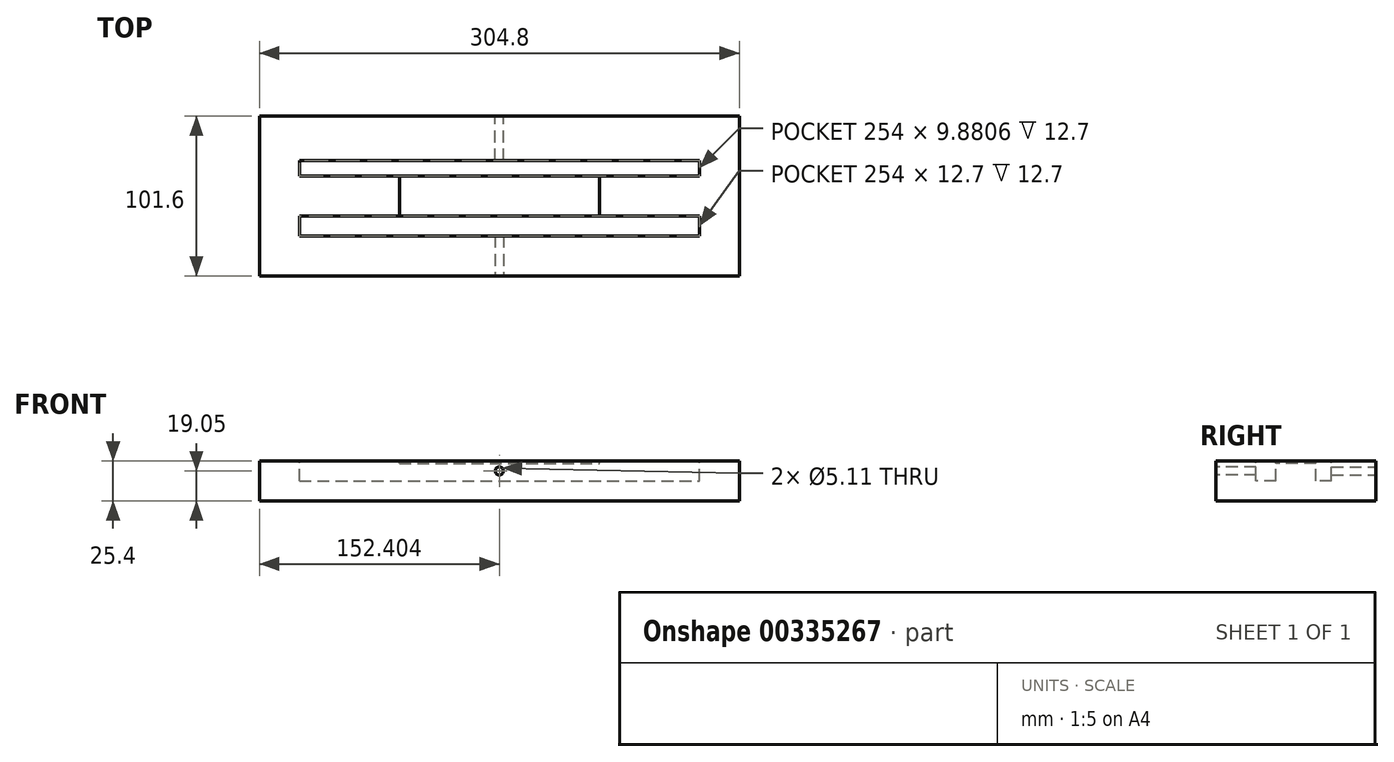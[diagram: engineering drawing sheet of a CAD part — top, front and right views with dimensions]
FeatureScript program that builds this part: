
annotation { "Feature Type Name" : "Feature", "Feature Type Description" : "" }
export const myFeature = defineFeature(function(context is Context, id is Id, definition is map)
    precondition{}
    {
        {
            var Q0;
            Q0=qCreatedBy(makeId("Top.planeOp"),FACE);
            var sketch = newSketch(context, id + "F0", { "sketchPlane" : qUnion([Q0])});
            skLineSegment(sketch, "E0.bottom", {"start": v(-47.49, 78.54) * mm, "end": v(257.31, 78.54) * mm});
            skLineSegment(sketch, "E0.top", {"start": v(-47.49, -23.06) * mm, "end": v(257.31, -23.06) * mm});
            skLineSegment(sketch, "E0.left", {"start": v(-47.49, 78.54) * mm, "end": v(-47.49, -23.06) * mm});
            skLineSegment(sketch, "E0.right", {"start": v(257.31, 78.54) * mm, "end": v(257.31, -23.06) * mm});
            skSolve(sketch);
        }
        {
            var Q0;
            Q0=makeQuery(id+"F0.imprint","IMPRINT",FACE,{"disambiguationData":[TD([[makeQuery(id+"F0.imprint","IMPRINT",EDGE,{"derivedFrom":sQuery(id+"F0.wireOp",EDGE,"E0.bottom")}),-1.0]])]});
            extrude(context, id + "F1", {"entities" : qUnion([Q0]), "depth" : 25.4 * mm});
        }
        {
            var Q0;
            Q0=makeQuery(id+"F1.opExtrude","CAP_FACE",FACE,{"disambiguationData":[OSD([sQuery(id+"F0.wireOp",EDGE,"E0.bottom"),sQuery(id+"F0.wireOp",EDGE,"E0.top"),sQuery(id+"F0.wireOp",EDGE,"E0.left"),sQuery(id+"F0.wireOp",EDGE,"E0.right")])],"isStart":false});
            var sketch = newSketch(context, id + "F2", { "sketchPlane" : qUnion([Q0])});
            skLineSegment(sketch, "E1.bottom", {"start": v(41.41, 40.44) * mm, "end": v(168.41, 40.44) * mm});
            skLineSegment(sketch, "E1.top", {"start": v(41.41, 15.04) * mm, "end": v(168.41, 15.04) * mm});
            skLineSegment(sketch, "E1.left", {"start": v(41.41, 40.44) * mm, "end": v(41.41, 15.04) * mm});
            skLineSegment(sketch, "E1.right", {"start": v(168.41, 40.44) * mm, "end": v(168.41, 15.04) * mm});
            skSolve(sketch);
        }
        {
            var Q0;
            Q0 = qSketchRegion(id + "F2", true);
            extrude(context, id + "F3", {"entities" : qUnion([Q0]), "operationType" : NewBodyOperationType.REMOVE, "oppositeDirection" : true, "depth" : 1.52 * mm});
        }
        {
            var Q0;
            Q0=makeQuery(id+"F1.opExtrude","CAP_FACE",FACE,{"disambiguationData":[OSD([sQuery(id+"F0.wireOp",EDGE,"E0.bottom"),sQuery(id+"F0.wireOp",EDGE,"E0.top"),sQuery(id+"F0.wireOp",EDGE,"E0.left"),sQuery(id+"F0.wireOp",EDGE,"E0.right")])],"isStart":false});
            var sketch = newSketch(context, id + "F4", { "sketchPlane" : qUnion([Q0])});
            skLineSegment(sketch, "E2.bottom", {"start": v(-22.09, 50.32) * mm, "end": v(231.91, 50.32) * mm});
            skLineSegment(sketch, "E2.top", {"start": v(-22.09, 40.44) * mm, "end": v(231.91, 40.44) * mm});
            skLineSegment(sketch, "E2.left", {"start": v(-22.09, 50.32) * mm, "end": v(-22.09, 40.44) * mm});
            skLineSegment(sketch, "E2.right", {"start": v(231.91, 50.32) * mm, "end": v(231.91, 40.44) * mm});
            skSolve(sketch);
        }
        {
            var Q0;
            Q0 = qSketchRegion(id + "F4", true);
            extrude(context, id + "F5", {"entities" : qUnion([Q0]), "operationType" : NewBodyOperationType.REMOVE, "oppositeDirection" : true, "depth" : 12.7 * mm});
        }
        {
            var Q0;
            Q0=makeQuery(id+"F1.opExtrude","CAP_FACE",FACE,{"disambiguationData":[OSD([sQuery(id+"F0.wireOp",EDGE,"E0.bottom"),sQuery(id+"F0.wireOp",EDGE,"E0.top"),sQuery(id+"F0.wireOp",EDGE,"E0.left"),sQuery(id+"F0.wireOp",EDGE,"E0.right")])],"isStart":false});
            var sketch = newSketch(context, id + "F6", { "sketchPlane" : qUnion([Q0])});
            skLineSegment(sketch, "E3.bottom", {"start": v(-22.09, 15.04) * mm, "end": v(231.91, 15.04) * mm});
            skLineSegment(sketch, "E3.top", {"start": v(-22.09, 2.34) * mm, "end": v(231.91, 2.34) * mm});
            skLineSegment(sketch, "E3.left", {"start": v(-22.09, 15.04) * mm, "end": v(-22.09, 2.34) * mm});
            skLineSegment(sketch, "E3.right", {"start": v(231.91, 15.04) * mm, "end": v(231.91, 2.34) * mm});
            skSolve(sketch);
        }
        {
            var Q0;
            Q0=makeQuery(id+"F6.imprint","IMPRINT",FACE,{"disambiguationData":[TD([[makeQuery(id+"F6.imprint","IMPRINT",EDGE,{"derivedFrom":sQuery(id+"F6.wireOp",EDGE,"E3.top")}),1.0]])]});
            extrude(context, id + "F7", {"entities" : qUnion([Q0]), "operationType" : NewBodyOperationType.REMOVE, "oppositeDirection" : true, "depth" : 12.7 * mm});
        }
        {
            var Q0;
            Q0=makeQuery(id+"F1.opExtrude","SWEPT_FACE",FACE,{"disambiguationData":[OSD([sQuery(id+"F0.wireOp",EDGE,"E0.top")])]});
            var sketch = newSketch(context, id + "F8", { "sketchPlane" : qUnion([Q0])});
            skPoint(sketch, "E4", {"position": v(104.91, 19.05) * mm});
            skPoint(sketch, "E4.positionSnap0", {"position": v(104.91, 25.4) * mm});
            skSolve(sketch);
        }
        {
            var Q0;
            Q0=sQuery(id+"F8.wireOp",VERTEX,"E4");
            var Q1;
            Q1=makeQuery(id+"F1.opExtrude","SWEPT_BODY",BODY,{"disambiguationData":[OSD([sQuery(id+"F0.wireOp",EDGE,"E0.bottom"),sQuery(id+"F0.wireOp",EDGE,"E0.top"),sQuery(id+"F0.wireOp",EDGE,"E0.left"),sQuery(id+"F0.wireOp",EDGE,"E0.right")])]});
            hole(context, id + "F9", {"style" : HoleStyle.SIMPLE, "endStyle" : HoleEndStyle.BLIND, "standardTappedOrClearance" : lookupTablePath({ "standard" : "ANSI", "engagement" : "75%", "pitch" : "20 tpi", "size" : "1/4", "type" : "Tapped" }), "standardBlindInLast" : lookupTablePath({ "standard" : "ANSI", "engagement" : "75%", "pitch" : "20 tpi", "size" : "1/4", "type" : "Tapped" }), "holeDiameter" : 5.1 * mm, "showTappedDepth" : true, "holeDepth" : 25.4 * mm, "tappedDepth" : 21.59 * mm, "tapClearance" : 3, "locations" : qUnion([Q0]), "scope" : qUnion([Q1]), "majorDiameter" : 6.35 * mm});
        }
        {
            var Q0;
            Q0=makeQuery(id+"F1.opExtrude","SWEPT_FACE",FACE,{"disambiguationData":[OSD([sQuery(id+"F0.wireOp",EDGE,"E0.bottom")])]});
            var sketch = newSketch(context, id + "F10", { "sketchPlane" : qUnion([Q0])});
            skPoint(sketch, "E5", {"position": v(-104.91, 19.05) * mm});
            skPoint(sketch, "E5.positionSnap0", {"position": v(-104.91, 25.4) * mm});
            skSolve(sketch);
        }
        {
            var Q0;
            Q0=sQuery(id+"F10.wireOp",VERTEX,"E5");
            var Q1;
            Q1=makeQuery(id+"F1.opExtrude","SWEPT_BODY",BODY,{"disambiguationData":[OSD([sQuery(id+"F0.wireOp",EDGE,"E0.bottom"),sQuery(id+"F0.wireOp",EDGE,"E0.top"),sQuery(id+"F0.wireOp",EDGE,"E0.left"),sQuery(id+"F0.wireOp",EDGE,"E0.right")])]});
            hole(context, id + "F11", {"style" : HoleStyle.SIMPLE, "endStyle" : HoleEndStyle.BLIND, "standardTappedOrClearance" : lookupTablePath({ "standard" : "ANSI", "engagement" : "75%", "pitch" : "20 tpi", "size" : "1/4", "type" : "Tapped" }), "standardBlindInLast" : lookupTablePath({ "standard" : "ANSI", "engagement" : "75%", "pitch" : "20 tpi", "size" : "1/4", "type" : "Tapped" }), "holeDiameter" : 5.1 * mm, "showTappedDepth" : true, "holeDepth" : 28.45 * mm, "tappedDepth" : 24.64 * mm, "tapClearance" : 3, "locations" : qUnion([Q0]), "scope" : qUnion([Q1]), "majorDiameter" : 6.35 * mm});
        }
    });
